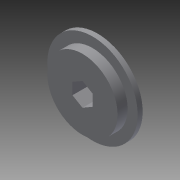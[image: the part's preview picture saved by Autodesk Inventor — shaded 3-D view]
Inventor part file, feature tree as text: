
AUTODESK INVENTOR PART (.ipt)
format: ipt  version: 2014 SP1 (Build 180222100, 222)  size: 98,304 bytes
history: native  units: in
note: dims shown in document units (in); Inventor stores cm internally (conversion verified against a paired STEP export)
features: extrude x2, sketch x2
ambient origin geometry x8: Origin, YZ Plane, XZ Plane, XY Plane, X Axis, Y Axis, Z Axis, Center Point
bodies: Solid1 (feature_tree)
feature tree (4):
  extrude  "Extrusion1"  Depth=0.5in
  extrude  "Extrusion3"  Depth=0.25in
  sketch  "Sketch1"  dims[d0=2.25in d1=0.5in]
  sketch  "Sketch3"  dims[d2=0.125in d3=0.0in d8=1.75in d9=0.25in d10=0.0in]
